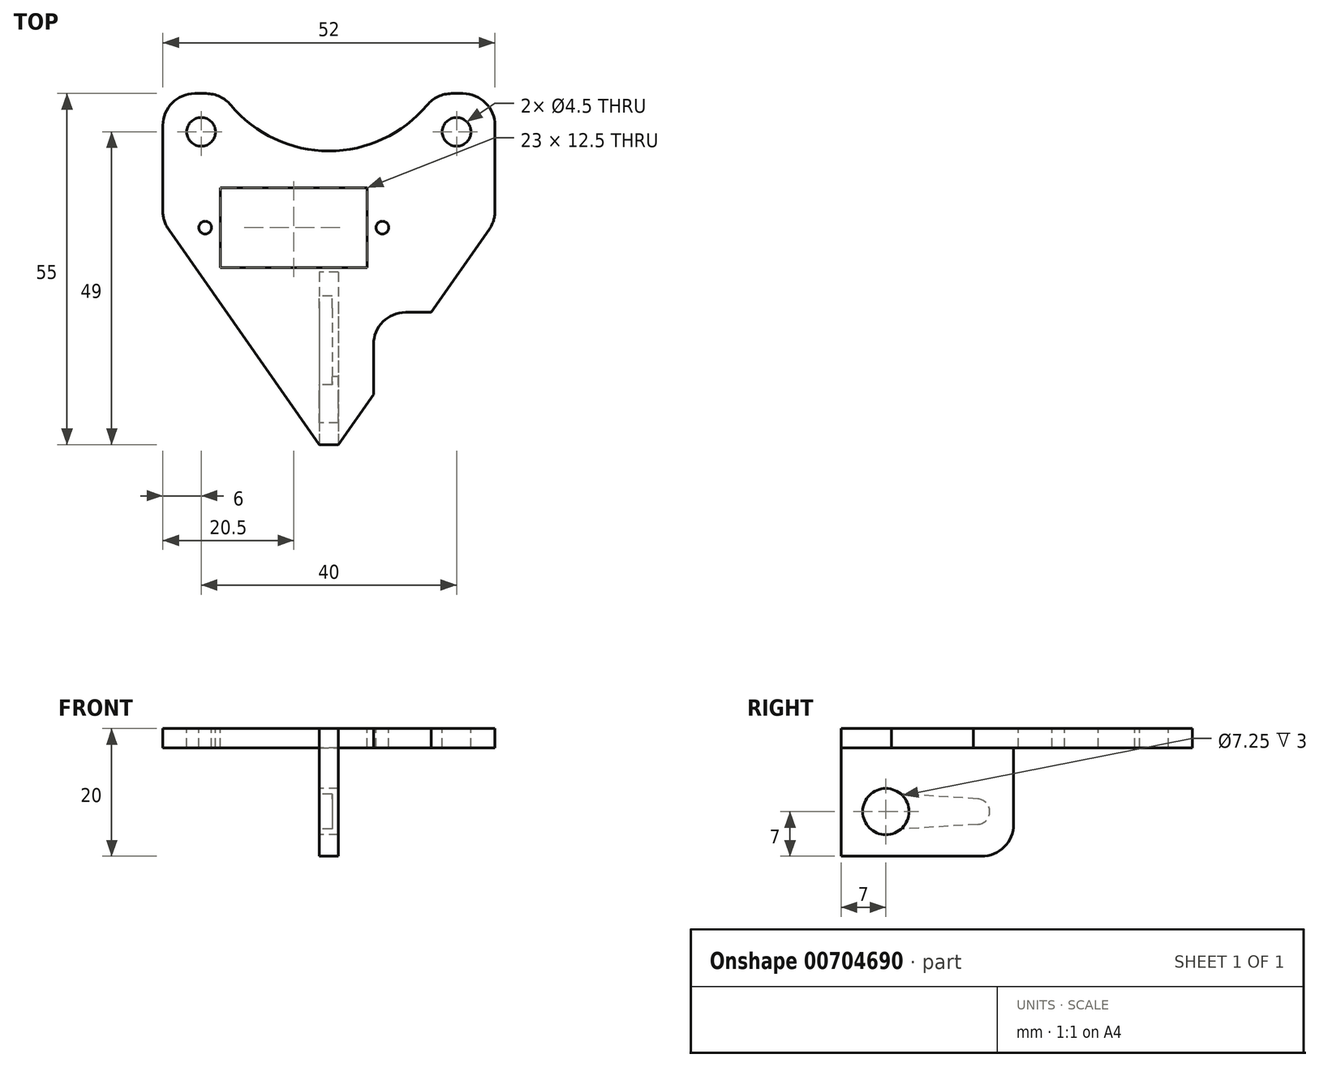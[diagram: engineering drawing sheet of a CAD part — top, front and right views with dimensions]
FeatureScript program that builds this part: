
annotation { "Feature Type Name" : "Feature", "Feature Type Description" : "" }
export const myFeature = defineFeature(function(context is Context, id is Id, definition is map)
    precondition{}
    {
        {
            var Q0;
            Q0=qCreatedBy(makeId("Top.planeOp"),FACE);
            var sketch = newSketch(context, id + "F0", { "sketchPlane" : qUnion([Q0])});
            skLineSegment(sketch, "E0.bottom", {"start": v(-26, 35) * mm, "end": v(26, 35) * mm});
            skLineSegment(sketch, "E0.top", {"start": v(-26, -20) * mm, "end": v(26, -20) * mm});
            skLineSegment(sketch, "E0.left", {"start": v(-26, 35) * mm, "end": v(-26, -20) * mm});
            skLineSegment(sketch, "E0.right", {"start": v(26, 35) * mm, "end": v(26, -20) * mm});
            skLineSegment(sketch, "E1.bottom", {"start": v(6, 7.75) * mm, "end": v(-17, 7.75) * mm});
            skLineSegment(sketch, "E1.top", {"start": v(6, 20.25) * mm, "end": v(-17, 20.25) * mm});
            skLineSegment(sketch, "E1.left", {"start": v(6, 7.75) * mm, "end": v(6, 20.25) * mm});
            skLineSegment(sketch, "E1.right", {"start": v(-17, 7.75) * mm, "end": v(-17, 20.25) * mm});
            skCircle(sketch, "E2", {"center": v(-19.38, 14) * mm, "radius": 1 * mm});
            skPoint(sketch, "E2.centerSnap0", {"position": v(-17, 14) * mm});
            skCircle(sketch, "E3", {"center": v(8.38, 14) * mm, "radius": 1 * mm});
            skCircle(sketch, "E4", {"center": v(20, 29) * mm, "radius": 2.25 * mm});
            skCircle(sketch, "E5", {"center": v(-20, 29) * mm, "radius": 2.25 * mm});
            skLineSegment(sketch, "E6.bottom", {"start": v(1.5, 7) * mm, "end": v(-1.5, 7) * mm});
            skLineSegment(sketch, "E6.top", {"start": v(1.5, -20) * mm, "end": v(-1.5, -20) * mm});
            skLineSegment(sketch, "E6.left", {"start": v(1.5, 7) * mm, "end": v(1.5, -20) * mm});
            skLineSegment(sketch, "E6.right", {"start": v(-1.5, 7) * mm, "end": v(-1.5, -20) * mm});
            skLineSegment(sketch, "E7", {"start": v(-17, 14) * mm, "end": v(6, 14) * mm, "construction": true});
            skCircle(sketch, "E8", {"center": v(0, 14) * mm, "radius": 3 * mm});
            skCircle(sketch, "E9", {"center": v(0, 46) * mm, "radius": 20 * mm});
            skSolve(sketch);
        }
        {
            var Q0;
            {var subQ0=sQuery(id+"F0.wireOp",EDGE,"E0.right");Q0=makeQuery(id+"F0.imprint","IMPRINT",FACE,{"disambiguationData":[TD([[makeQuery(id+"F0.imprint","IMPRINT",EDGE,{"derivedFrom":subQ0}),-1.0]])]});}
            var Q1;
            {var subQ0=sQuery(id+"F0.wireOp",EDGE,"E0.left");Q1=makeQuery(id+"F0.imprint","IMPRINT",FACE,{"disambiguationData":[TD([[makeQuery(id+"F0.imprint","IMPRINT",EDGE,{"derivedFrom":subQ0}),1.0]])]});}
            var Q2;
            Q2=makeQuery(id+"F0.imprint","IMPRINT",FACE,{"disambiguationData":[TD([[makeQuery(id+"F0.imprint","IMPRINT",EDGE,{"derivedFrom":sQuery(id+"F0.wireOp",EDGE,"E6.bottom")}),1.0]])]});
            var Q3;
            {var subQ5=sQuery(id+"F0.wireOp",EDGE,"E6.bottom");Q3=makeQuery(id+"F0.imprint","IMPRINT",FACE,{"disambiguationData":[TD([[makeQuery(id+"F0.imprint","IMPRINT",EDGE,{"derivedFrom":subQ5}),-1.0]])]});}
            extrude(context, id + "F1", {"entities" : qUnion([Q0, Q1, Q2, Q3]), "oppositeDirection" : true, "depth" : 3 * mm, "offsetDistance" : 25 * mm});
        }
        {
            var Q0;
            Q0=makeQuery(id+"F0.imprint","IMPRINT",FACE,{"disambiguationData":[TD([[makeQuery(id+"F0.imprint","IMPRINT",EDGE,{"derivedFrom":sQuery(id+"F0.wireOp",EDGE,"E6.bottom")}),1.0]])]});
            extrude(context, id + "F2", {"entities" : qUnion([Q0]), "operationType" : NewBodyOperationType.ADD, "oppositeDirection" : true, "depth" : 20 * mm, "offsetDistance" : 25 * mm});
        }
        {
            var Q0;
            Q0=makeQuery(id+"F1.opExtrude","SWEPT_EDGE",EDGE,{"disambiguationData":[OSD([sQuery(id+"F0.wireOp",EDGE,"E0.top"),sQuery(id+"F0.wireOp",EDGE,"E0.left")])]});
            var Q1;
            Q1=makeQuery(id+"F1.opExtrude","SWEPT_EDGE",EDGE,{"disambiguationData":[OSD([sQuery(id+"F0.wireOp",EDGE,"E0.top"),sQuery(id+"F0.wireOp",EDGE,"E0.right")])]});
            chamfer(context, id + "F3", {"entities" : qUnion([Q0, Q1]), "chamferType" : ChamferType.TWO_OFFSETS, "width1" : 35 * mm, "oppositeDirection" : false, "width2" : 24.5 * mm, "tangentPropagation" : true});
        }
        {
            var Q0;
            Q0=makeQuery(id+"F1.opExtrude","SWEPT_EDGE",EDGE,{"disambiguationData":[OSD([sQuery(id+"F0.wireOp",EDGE,"E0.bottom"),sQuery(id+"F0.wireOp",EDGE,"E0.left")])]});
            var Q1;
            Q1=makeQuery(id+"F1.opExtrude","SWEPT_EDGE",EDGE,{"disambiguationData":[OSD([sQuery(id+"F0.wireOp",EDGE,"E0.bottom"),sQuery(id+"F0.wireOp",EDGE,"E0.right")])]});
            fillet(context, id + "F4", {"entities" : qUnion([Q0, Q1]), "radius" : 5 * mm, "tangentPropagation" : true, "allowEdgeOverflow" : false});
        }
        {
            var Q0;
            Q0=makeQuery(id+"F2.opExtrude","SWEPT_FACE",FACE,{"disambiguationData":[OSD([sQuery(id+"F0.wireOp",EDGE,"E6.right")])]});
            var sketch = newSketch(context, id + "F5", { "sketchPlane" : qUnion([Q0])});
            skCircle(sketch, "E10", {"center": v(13, -13) * mm, "radius": 3.62 * mm});
            skCircle(sketch, "E11", {"center": v(-1.25, -13) * mm, "radius": 2 * mm});
            skLineSegment(sketch, "E12", {"start": v(-1.38, -15) * mm, "end": v(10.64, -15.75) * mm});
            skLineSegment(sketch, "E13", {"start": v(-1.38, -11) * mm, "end": v(10.64, -10.25) * mm});
            skLineSegment(sketch, "E14", {"start": v(-1.25, -13) * mm, "end": v(13, -13) * mm, "construction": true});
            skSolve(sketch);
        }
        {
            var Q0;
            {var subQ0=sQuery(id+"F5.wireOp",EDGE,"E10");var subQ1=makeQuery(id+"F5.imprint","INTERSECT",VERTEX,{"derivedFrom":[subQ0,sQuery(id+"F5.wireOp",EDGE,"E12")]});Q0=makeQuery(id+"F5.imprint","IMPRINT",FACE,{"disambiguationData":[TD([[makeQuery(id+"F5.imprint","IMPRINT",EDGE,{"disambiguationData":[TD([[subQ1,-1.0]])],"derivedFrom":subQ0}),1.0]])]});}
            extrude(context, id + "F6", {"entities" : qUnion([Q0]), "operationType" : NewBodyOperationType.REMOVE, "oppositeDirection" : true, "depth" : 25 * mm, "offsetDistance" : 25 * mm});
        }
        {
            var Q0;
            {var subQ0=sQuery(id+"F5.wireOp",EDGE,"E12");Q0=makeQuery(id+"F5.imprint","IMPRINT",FACE,{"disambiguationData":[TD([[makeQuery(id+"F5.imprint","IMPRINT",EDGE,{"derivedFrom":subQ0}),1.0]])]});}
            var Q1;
            {var subQ0=sQuery(id+"F5.wireOp",EDGE,"E11");var subQ1=makeQuery(id+"F5.imprint","INTERSECT",VERTEX,{"derivedFrom":[subQ0,sQuery(id+"F5.wireOp",EDGE,"E12")]});Q1=makeQuery(id+"F5.imprint","IMPRINT",FACE,{"disambiguationData":[TD([[makeQuery(id+"F5.imprint","IMPRINT",EDGE,{"disambiguationData":[TD([[subQ1,-1.0]])],"derivedFrom":subQ0}),1.0]])]});}
            extrude(context, id + "F7", {"entities" : qUnion([Q0, Q1]), "operationType" : NewBodyOperationType.REMOVE, "oppositeDirection" : true, "depth" : 2 * mm, "offsetDistance" : 25 * mm});
        }
        {
            var Q0;
            {var subQ0=sQuery(id+"F0.wireOp",EDGE,"E0.left");Q0=makeQuery(id+"F3.opChamfer","BLEND_EDGE",EDGE,{"blendedFrom":[makeQuery(id+"F1.opExtrude","SWEPT_EDGE",EDGE,{"disambiguationData":[OSD([sQuery(id+"F0.wireOp",EDGE,"E0.top"),subQ0])]}),makeQuery(id+"F1.opExtrude","SWEPT_FACE",FACE,{"disambiguationData":[OSD([subQ0])]})],"blendedInto":[makeQuery(id+"F1.opExtrude","SWEPT_FACE",FACE,{"disambiguationData":[OSD([subQ0])]})]});}
            var Q1;
            {var subQ0=sQuery(id+"F0.wireOp",EDGE,"E0.right");Q1=makeQuery(id+"F3.opChamfer","BLEND_EDGE",EDGE,{"blendedFrom":[makeQuery(id+"F1.opExtrude","SWEPT_EDGE",EDGE,{"disambiguationData":[OSD([sQuery(id+"F0.wireOp",EDGE,"E0.top"),subQ0])]}),makeQuery(id+"F1.opExtrude","SWEPT_FACE",FACE,{"disambiguationData":[OSD([subQ0])]})],"blendedInto":[makeQuery(id+"F1.opExtrude","SWEPT_FACE",FACE,{"disambiguationData":[OSD([subQ0])]})]});}
            fillet(context, id + "F8", {"entities" : qUnion([Q0, Q1]), "radius" : 5 * mm, "tangentPropagation" : true, "allowEdgeOverflow" : false});
        }
        {
            var Q0;
            {var subQ0=sQuery(id+"F0.wireOp",EDGE,"E9");var subQ1=sQuery(id+"F0.wireOp",EDGE,"E0.bottom");Q0=makeQuery(id+"F1.opExtrude","SWEPT_EDGE",EDGE,{"disambiguationData":[OSD([subQ1,subQ0]),TDD([makeQuery(id+"F0.imprint","INTERSECT",VERTEX,{"disambiguationData":[OD(0.0)],"derivedFrom":[subQ1,subQ0]})])]});}
            var Q1;
            {var subQ0=sQuery(id+"F0.wireOp",EDGE,"E9");var subQ1=sQuery(id+"F0.wireOp",EDGE,"E0.bottom");Q1=makeQuery(id+"F1.opExtrude","SWEPT_EDGE",EDGE,{"disambiguationData":[OSD([subQ1,subQ0]),TDD([makeQuery(id+"F0.imprint","INTERSECT",VERTEX,{"disambiguationData":[OD(1.0)],"derivedFrom":[subQ1,subQ0]})])]});}
            fillet(context, id + "F9", {"entities" : qUnion([Q0, Q1]), "radius" : 5 * mm, "tangentPropagation" : true, "allowEdgeOverflow" : false});
        }
        {
            var Q0;
            Q0=makeQuery(id+"F2.opExtrude","CAP_EDGE",EDGE,{"disambiguationData":[OSD([sQuery(id+"F0.wireOp",EDGE,"E6.top")])],"isStart":false});
            var Q1;
            Q1=makeQuery(id+"F2.opExtrude","CAP_EDGE",EDGE,{"disambiguationData":[OSD([sQuery(id+"F0.wireOp",EDGE,"E6.bottom")])],"isStart":false});
            fillet(context, id + "F10", {"entities" : qUnion([Q0, Q1]), "radius" : 5 * mm, "tangentPropagation" : true, "allowEdgeOverflow" : false});
        }
        {
            var Q0;
            Q0=makeQuery(id+"F1.opExtrude","CAP_FACE",FACE,{"disambiguationData":[OSD([sQuery(id+"F0.wireOp",EDGE,"E0.bottom"),sQuery(id+"F0.wireOp",EDGE,"E0.top"),sQuery(id+"F0.wireOp",EDGE,"E0.left"),sQuery(id+"F0.wireOp",EDGE,"E0.right"),sQuery(id+"F0.wireOp",EDGE,"E1.bottom"),sQuery(id+"F0.wireOp",EDGE,"E1.top"),sQuery(id+"F0.wireOp",EDGE,"E1.left"),sQuery(id+"F0.wireOp",EDGE,"E1.right"),sQuery(id+"F0.wireOp",EDGE,"E2"),sQuery(id+"F0.wireOp",EDGE,"E3"),sQuery(id+"F0.wireOp",EDGE,"E4"),sQuery(id+"F0.wireOp",EDGE,"E5"),sQuery(id+"F0.wireOp",EDGE,"E6.top"),sQuery(id+"F0.wireOp",EDGE,"E9")])],"isStart":true});
            var sketch = newSketch(context, id + "F11", { "sketchPlane" : qUnion([Q0])});
            skLineSegment(sketch, "E15.bottom", {"start": v(7, -12.14) * mm, "end": v(16, -12.14) * mm});
            skLineSegment(sketch, "E15.top", {"start": v(7, 0.71) * mm, "end": v(16, 0.71) * mm});
            skLineSegment(sketch, "E15.left", {"start": v(7, -12.14) * mm, "end": v(7, 0.71) * mm});
            skLineSegment(sketch, "E15.right", {"start": v(16, -12.14) * mm, "end": v(16, 0.71) * mm});
            skSolve(sketch);
        }
        {
            var Q0;
            {var subQ0=sQuery(id+"F11.wireOp",EDGE,"E15.top");Q0=makeQuery(id+"F11.imprint","IMPRINT",FACE,{"disambiguationData":[TD([[makeQuery(id+"F11.imprint","IMPRINT",EDGE,{"derivedFrom":subQ0}),-1.0]])]});}
            extrude(context, id + "F12", {"entities" : qUnion([Q0]), "operationType" : NewBodyOperationType.REMOVE, "oppositeDirection" : true, "depth" : 25 * mm, "offsetDistance" : 25 * mm});
        }
        {
            var Q0;
            Q0=makeQuery(id+"F12.boolean.opBoolean","COPY",EDGE,{"derivedFrom":makeQuery(id+"F12.opExtrude","SWEPT_EDGE",EDGE,{"disambiguationData":[OSD([sQuery(id+"F0.wireOp",EDGE,"E0.bottom"),sQuery(id+"F0.wireOp",EDGE,"E0.top"),sQuery(id+"F0.wireOp",EDGE,"E0.left"),sQuery(id+"F0.wireOp",EDGE,"E0.right"),sQuery(id+"F0.wireOp",EDGE,"E1.bottom"),sQuery(id+"F0.wireOp",EDGE,"E1.top"),sQuery(id+"F0.wireOp",EDGE,"E1.left"),sQuery(id+"F0.wireOp",EDGE,"E1.right"),sQuery(id+"F0.wireOp",EDGE,"E2"),sQuery(id+"F0.wireOp",EDGE,"E3"),sQuery(id+"F0.wireOp",EDGE,"E4"),sQuery(id+"F0.wireOp",EDGE,"E5"),sQuery(id+"F0.wireOp",EDGE,"E6.top"),sQuery(id+"F0.wireOp",EDGE,"E9"),sQuery(id+"F11.wireOp",EDGE,"E15.top"),sQuery(id+"F11.wireOp",EDGE,"E15.right")])]})});
            var Q1;
            Q1=makeQuery(id+"F12.boolean.opBoolean","COPY",EDGE,{"derivedFrom":makeQuery(id+"F12.opExtrude","SWEPT_EDGE",EDGE,{"disambiguationData":[OSD([sQuery(id+"F11.wireOp",EDGE,"E15.top"),sQuery(id+"F11.wireOp",EDGE,"E15.left")])]})});
            var Q2;
            Q2=makeQuery(id+"F12.boolean.opBoolean","COPY",EDGE,{"derivedFrom":makeQuery(id+"F12.opExtrude","SWEPT_EDGE",EDGE,{"disambiguationData":[OSD([sQuery(id+"F0.wireOp",EDGE,"E0.bottom"),sQuery(id+"F0.wireOp",EDGE,"E0.top"),sQuery(id+"F0.wireOp",EDGE,"E0.left"),sQuery(id+"F0.wireOp",EDGE,"E0.right"),sQuery(id+"F0.wireOp",EDGE,"E1.bottom"),sQuery(id+"F0.wireOp",EDGE,"E1.top"),sQuery(id+"F0.wireOp",EDGE,"E1.left"),sQuery(id+"F0.wireOp",EDGE,"E1.right"),sQuery(id+"F0.wireOp",EDGE,"E2"),sQuery(id+"F0.wireOp",EDGE,"E3"),sQuery(id+"F0.wireOp",EDGE,"E4"),sQuery(id+"F0.wireOp",EDGE,"E5"),sQuery(id+"F0.wireOp",EDGE,"E6.top"),sQuery(id+"F0.wireOp",EDGE,"E9"),sQuery(id+"F11.wireOp",EDGE,"E15.bottom"),sQuery(id+"F11.wireOp",EDGE,"E15.left")])]})});
            fillet(context, id + "F13", {"entities" : qUnion([Q0, Q1, Q2]), "radius" : 5 * mm, "tangentPropagation" : true, "allowEdgeOverflow" : false});
        }
    });
